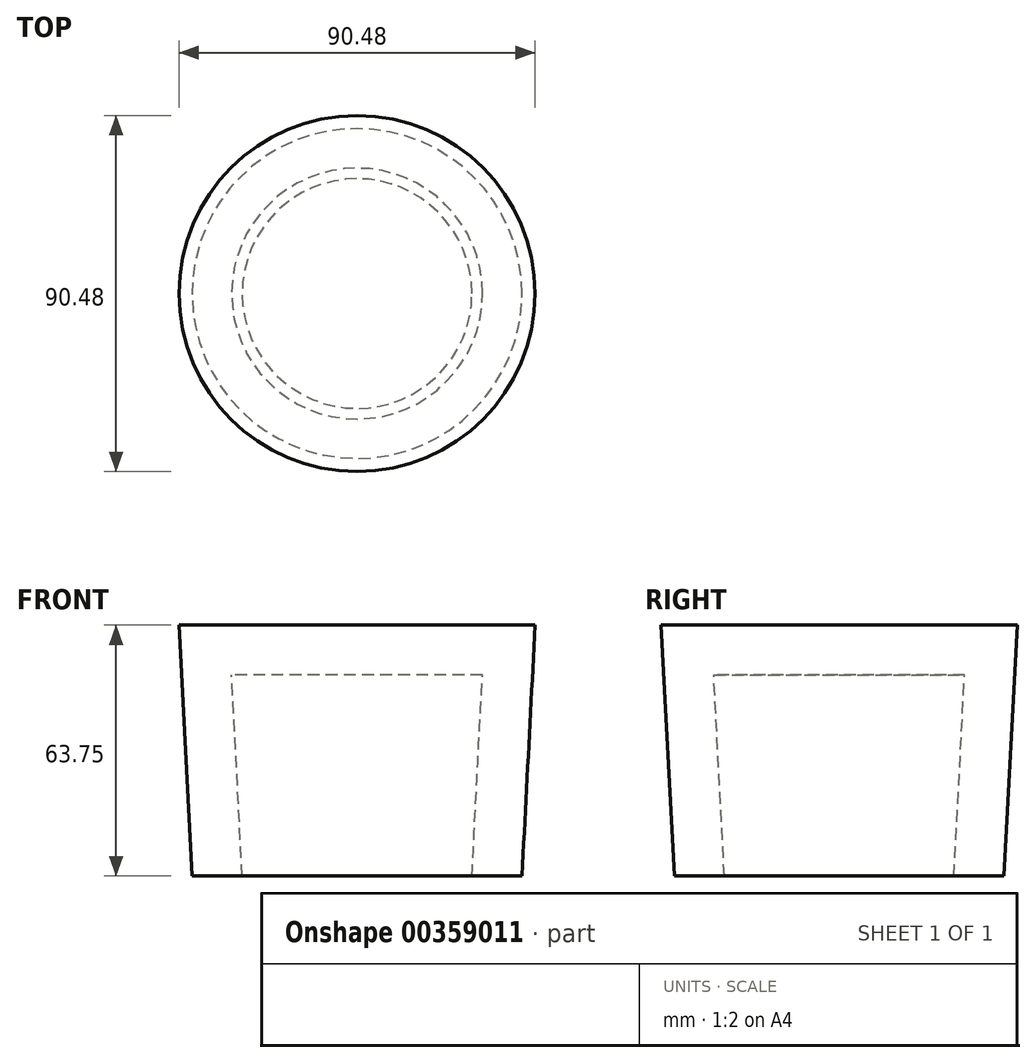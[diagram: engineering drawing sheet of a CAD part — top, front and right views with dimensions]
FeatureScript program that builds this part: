
annotation { "Feature Type Name" : "Feature", "Feature Type Description" : "" }
export const myFeature = defineFeature(function(context is Context, id is Id, definition is map)
    precondition{}
    {
        {
            var Q0;
            Q0=qCreatedBy(makeId("Top.planeOp"),FACE);
            var sketch = newSketch(context, id + "F0", { "sketchPlane" : qUnion([Q0])});
            skCircle(sketch, "E0", {"center": v(0, 0) * mm, "radius": 45.24 * mm});
            skSolve(sketch);
        }
        {
            var Q0;
            Q0=makeQuery(id+"F0.imprint","IMPRINT",FACE,{"disambiguationData":[TD([[makeQuery(id+"F0.imprint","IMPRINT",EDGE,{"derivedFrom":sQuery(id+"F0.wireOp",EDGE,"E0")}),1.0]])]});
            extrude(context, id + "F1", {"entities" : qUnion([Q0]), "oppositeDirection" : true, "depth" : 63.75 * mm, "hasDraft" : true, "draftAngle" : 3 * degree, "draftPullDirection" : true});
        }
        {
            var Q0;
            Q0=makeQuery(id+"F1.opExtrude","CAP_FACE",FACE,{"disambiguationData":[OSD([sQuery(id+"F0.wireOp",EDGE,"E0")])],"isStart":false});
            shell(context, id + "F2", {"entities" : qUnion([Q0]), "thickness" : 12.7 * mm});
        }
    });
